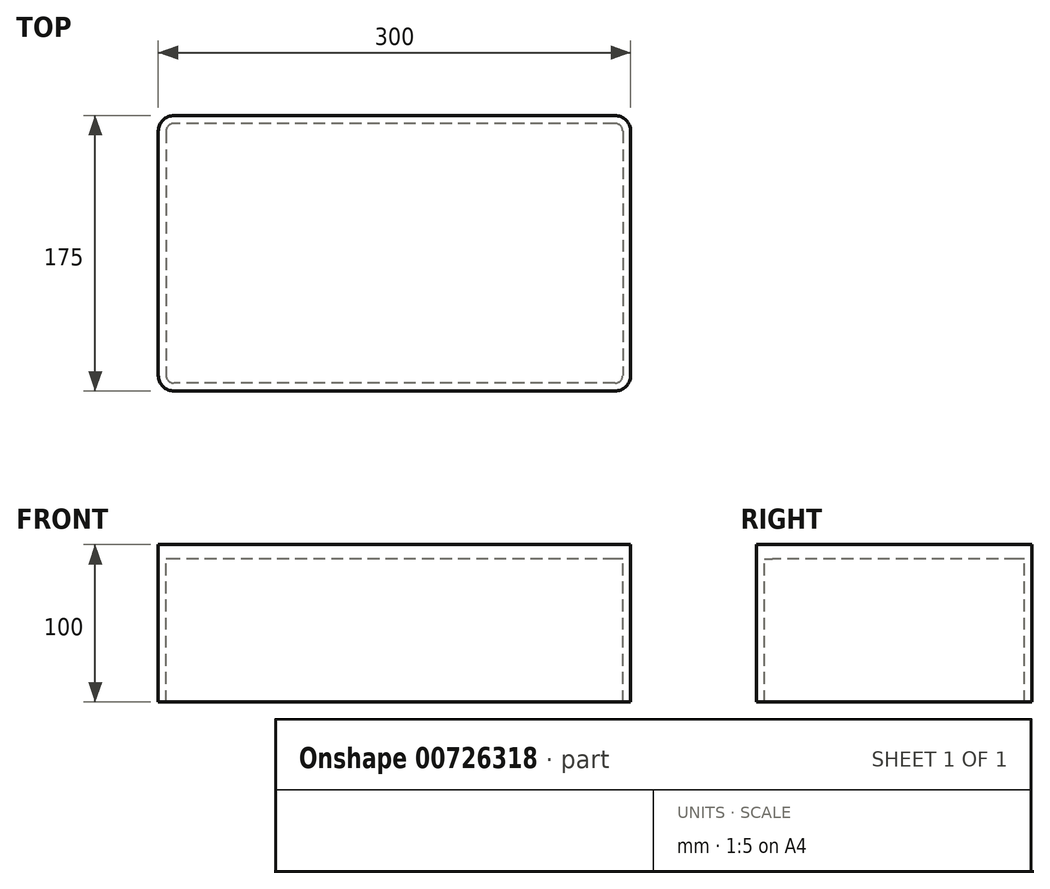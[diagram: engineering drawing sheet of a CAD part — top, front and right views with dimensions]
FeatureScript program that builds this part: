
annotation { "Feature Type Name" : "Feature", "Feature Type Description" : "" }
export const myFeature = defineFeature(function(context is Context, id is Id, definition is map)
    precondition{}
    {
        {
            var Q0;
            Q0=qCreatedBy(makeId("Top.planeOp"),FACE);
            var sketch = newSketch(context, id + "F0", { "sketchPlane" : qUnion([Q0])});
            skLineSegment(sketch, "E0.bottom", {"start": v(140, 87.5) * mm, "end": v(-140, 87.5) * mm});
            skLineSegment(sketch, "E0.top", {"start": v(140, -87.5) * mm, "end": v(-140, -87.5) * mm});
            skLineSegment(sketch, "E0.left", {"start": v(150, 77.5) * mm, "end": v(150, -77.5) * mm});
            skLineSegment(sketch, "E0.right", {"start": v(-150, 77.5) * mm, "end": v(-150, -77.5) * mm});
            skPoint(sketch, "E0.middle", {"position": v(0, 0) * mm});
            skPoint(sketch, "E1.visualSharp", {"position": v(150, 87.5) * mm});
            skArc(sketch, "E1.filletArc", {"start": v(150, 77.5) * mm, "mid": v(147.07, 84.57) * mm, "end": v(140, 87.5) * mm});
            skPoint(sketch, "E2.visualSharp", {"position": v(150, -87.5) * mm});
            skArc(sketch, "E2.filletArc", {"start": v(140, -87.5) * mm, "mid": v(147.07, -84.57) * mm, "end": v(150, -77.5) * mm});
            skPoint(sketch, "E3.visualSharp", {"position": v(-150, 87.5) * mm});
            skArc(sketch, "E3.filletArc", {"start": v(-140, 87.5) * mm, "mid": v(-147.07, 84.57) * mm, "end": v(-150, 77.5) * mm});
            skPoint(sketch, "E4.visualSharp", {"position": v(-150, -87.5) * mm});
            skArc(sketch, "E4.filletArc", {"start": v(-150, -77.5) * mm, "mid": v(-147.07, -84.57) * mm, "end": v(-140, -87.5) * mm});
            skLineSegment(sketch, "E5.0", {"start": v(145, 77.5) * mm, "end": v(145, -77.5) * mm});
            skArc(sketch, "E5.1", {"start": v(145, 77.5) * mm, "mid": v(143.54, 81.04) * mm, "end": v(140, 82.5) * mm});
            skLineSegment(sketch, "E5.2", {"start": v(140, 82.5) * mm, "end": v(-140, 82.5) * mm});
            skLineSegment(sketch, "E5.3", {"start": v(140, -82.5) * mm, "end": v(-140, -82.5) * mm});
            skArc(sketch, "E5.4", {"start": v(-145, -77.5) * mm, "mid": v(-143.54, -81.04) * mm, "end": v(-140, -82.5) * mm});
            skLineSegment(sketch, "E5.5", {"start": v(-145, 77.5) * mm, "end": v(-145, -77.5) * mm});
            skArc(sketch, "E5.6", {"start": v(-140, 82.5) * mm, "mid": v(-143.54, 81.04) * mm, "end": v(-145, 77.5) * mm});
            skArc(sketch, "E6.0", {"start": v(140, -82.5) * mm, "mid": v(143.54, -81.04) * mm, "end": v(145, -77.5) * mm});
            skSolve(sketch);
        }
        {
            var Q0;
            Q0=makeQuery(id+"F0.imprint","IMPRINT",FACE,{"disambiguationData":[TD([[makeQuery(id+"F0.imprint","IMPRINT",EDGE,{"derivedFrom":sQuery(id+"F0.wireOp",EDGE,"E0.bottom")}),1.0]])]});
            extrude(context, id + "F1", {"entities" : qUnion([Q0]), "oppositeDirection" : true, "depth" : 100 * mm, "offsetDistance" : 25 * mm});
        }
        {
            var Q0;
            Q0=makeQuery(id+"F0.imprint","IMPRINT",FACE,{"disambiguationData":[TD([[makeQuery(id+"F0.imprint","IMPRINT",EDGE,{"derivedFrom":sQuery(id+"F0.wireOp",EDGE,"E5.0")}),-1.0]])]});
            extrude(context, id + "F2", {"entities" : qUnion([Q0]), "operationType" : NewBodyOperationType.ADD, "oppositeDirection" : true, "depth" : 9 * mm, "offsetDistance" : 25 * mm});
        }
    });
